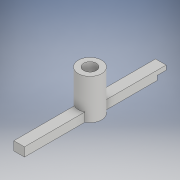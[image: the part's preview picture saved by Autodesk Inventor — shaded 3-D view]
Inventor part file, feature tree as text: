
AUTODESK INVENTOR PART (.ipt)
format: ipt  version: 2019 (Build 230136000, 136)  size: 160,768 bytes
history: native  units: in
note: dims shown in document units (in); Inventor stores cm internally (conversion verified against a paired STEP export)
features: sketch x7, extrude x6, projected_geometry x3
ambient origin geometry x8: Origin, YZ Plane, XZ Plane, XY Plane, X Axis, Y Axis, Z Axis, Center Point
bodies: Solid1 (feature_tree)
feature tree (16):
  extrude  "Extrusion1"  Depth=0.36in
  extrude  "Extrusion2"  Depth=0.1in TaperAngle=0.0deg
  extrude  "Extrusion7"  TaperAngle=0.0deg  [1 undecoded]
  extrude  "Extrusion18"  TaperAngle=0.0deg  [1 undecoded]
  extrude  "Extrusion19"  Depth=4.0in
  extrude  "Extrusion20"  Depth=0.15in
  sketch  "Sketch27"  dims[d94=0.25in d95=0.0in d96=0.25in d97=0.0in d98=0.125in d99=0.25in d100=1.0in d101=0.0in]
  sketch  "Sketch1"  dims[d0=0.36in d1=0.15in]
  sketch  "Sketch2"  dims[d2=0.78in d3=0.0in d4=0.1in d5=0.0in]
  sketch  "Sketch10"  dims[d28=0.875in d29=0.0in d42=0.0in]
  sketch  "Sketch24"  dims[d43=0.0in d44=0.0in]
  projected_geometry  "Projected Loop15"
  sketch  "Sketch25"  dims[d90=4.0in d91=2.0in]
  projected_geometry  "Projected Loop16"
  projected_geometry  "Projected Loop17"
  sketch  "Sketch26"  dims[d92=0.15in d93=0.15in]
note: 2 required parameter values undecoded (feature->parameter linkage not recoverable at this tier; creation-order binding heuristic only, values carry confidence <= 0.55)
